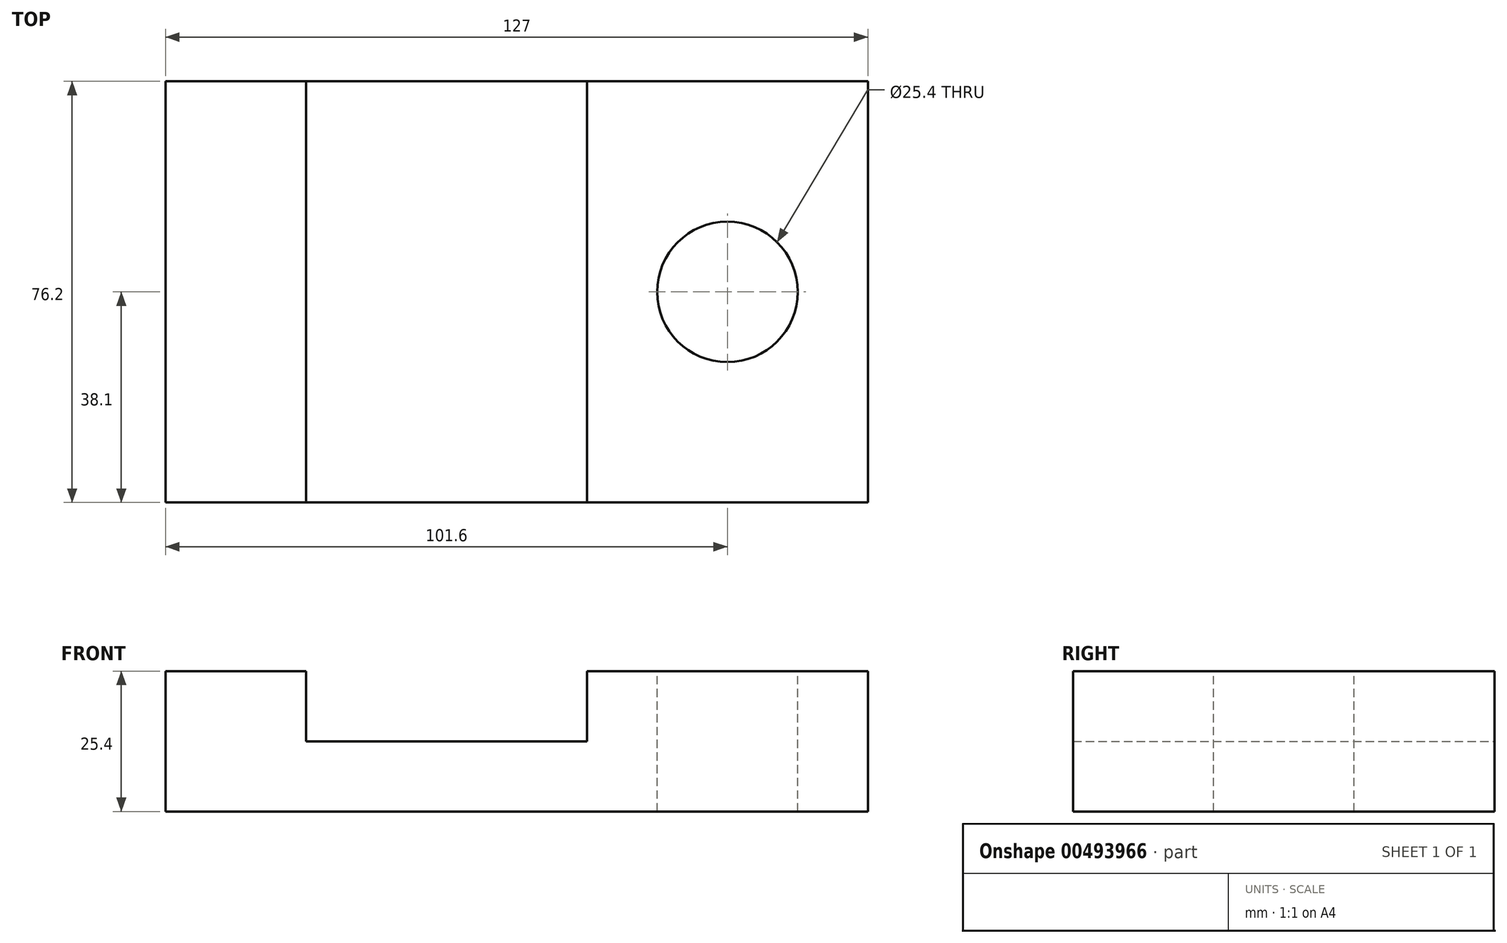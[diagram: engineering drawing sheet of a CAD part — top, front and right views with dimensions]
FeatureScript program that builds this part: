
annotation { "Feature Type Name" : "Feature", "Feature Type Description" : "" }
export const myFeature = defineFeature(function(context is Context, id is Id, definition is map)
    precondition{}
    {
        {
            var Q0;
            Q0=qCreatedBy(makeId("Front.planeOp"),FACE);
            var sketch = newSketch(context, id + "F0", { "sketchPlane" : qUnion([Q0])});
            skLineSegment(sketch, "E0", {"start": v(0, 0) * mm, "end": v(-127, 0) * mm});
            skLineSegment(sketch, "E1", {"start": v(-127, 0) * mm, "end": v(-127, 25.4) * mm});
            skLineSegment(sketch, "E2", {"start": v(-127, 25.4) * mm, "end": v(-101.6, 25.4) * mm});
            skLineSegment(sketch, "E3", {"start": v(-101.6, 25.4) * mm, "end": v(-101.6, 12.7) * mm});
            skLineSegment(sketch, "E4", {"start": v(-101.6, 12.7) * mm, "end": v(-50.8, 12.7) * mm});
            skLineSegment(sketch, "E5", {"start": v(-50.8, 12.7) * mm, "end": v(-50.8, 25.4) * mm});
            skLineSegment(sketch, "E6", {"start": v(-50.8, 25.4) * mm, "end": v(0, 25.4) * mm});
            skLineSegment(sketch, "E7", {"start": v(0, 25.4) * mm, "end": v(0, 0) * mm});
            skSolve(sketch);
        }
        {
            var Q0;
            Q0 = qSketchRegion(id + "F0", true);
            extrude(context, id + "F1", {"entities" : qUnion([Q0]), "endBound" : BoundingType.SYMMETRIC, "depth" : 76.2 * mm});
        }
        {
            var Q0;
            Q0=makeQuery(id+"F1.opExtrude","SWEPT_FACE",FACE,{"disambiguationData":[OSD([sQuery(id+"F0.wireOp",EDGE,"E6")])]});
            var sketch = newSketch(context, id + "F2", { "sketchPlane" : qUnion([Q0])});
            skCircle(sketch, "E8", {"center": v(-25.4, 0) * mm, "radius": 12.7 * mm});
            skSolve(sketch);
        }
        {
            var Q0;
            Q0 = qSketchRegion(id + "F2", true);
            extrude(context, id + "F3", {"entities" : qUnion([Q0]), "operationType" : NewBodyOperationType.REMOVE, "oppositeDirection" : true, "depth" : 25.4 * mm});
        }
    });
